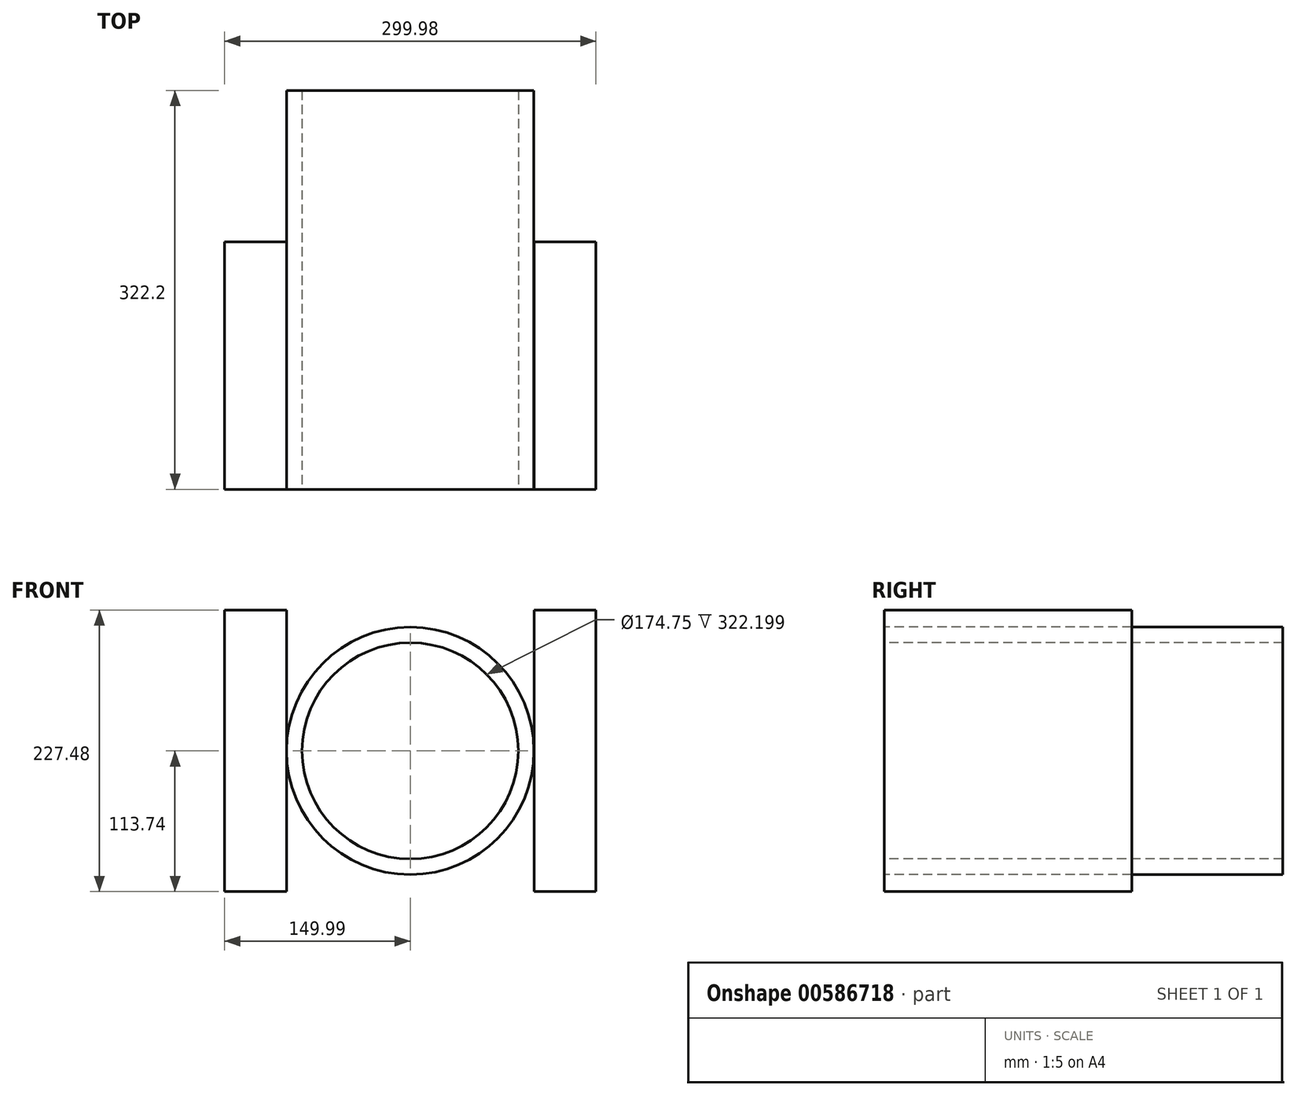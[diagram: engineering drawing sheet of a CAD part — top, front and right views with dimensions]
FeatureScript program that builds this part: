
annotation { "Feature Type Name" : "Feature", "Feature Type Description" : "" }
export const myFeature = defineFeature(function(context is Context, id is Id, definition is map)
    precondition{}
    {
        {
            var Q0;
            Q0=qCreatedBy(makeId("Front.planeOp"),FACE);
            var sketch = newSketch(context, id + "F0", { "sketchPlane" : qUnion([Q0])});
            skCircle(sketch, "E0", {"center": v(0, 0) * mm, "radius": 99.95 * mm});
            skSolve(sketch);
        }
        {
            var Q0;
            Q0=makeQuery(id+"F0.imprint","IMPRINT",FACE,{"disambiguationData":[TD([[makeQuery(id+"F0.imprint","IMPRINT",EDGE,{"derivedFrom":sQuery(id+"F0.wireOp",EDGE,"E0")}),1.0]])]});
            extrude(context, id + "F1", {"entities" : qUnion([Q0]), "oppositeDirection" : true, "depth" : 322.2 * mm, "offsetDistance" : 25.4 * mm});
        }
        {
            var Q0;
            Q0=qCreatedBy(makeId("Right.planeOp"),FACE);
            cPlane(context, id + "F2", {"entities" : qUnion([Q0]), "cplaneType" : CPlaneType.OFFSET, "offset" : 100 * mm, "width" : 152.4 * mm, "height" : 152.4 * mm});
        }
        {
            var Q0;
            Q0=qCreatedBy(id+"F2.planeOp",FACE);
            var sketch = newSketch(context, id + "F3", { "sketchPlane" : qUnion([Q0])});
            skLineSegment(sketch, "E1.bottom", {"start": v(0, 113.74) * mm, "end": v(200, 113.74) * mm});
            skLineSegment(sketch, "E1.top", {"start": v(0, -113.74) * mm, "end": v(200, -113.74) * mm});
            skLineSegment(sketch, "E1.left", {"start": v(0, 113.74) * mm, "end": v(0, -113.74) * mm});
            skLineSegment(sketch, "E1.right", {"start": v(200, 113.74) * mm, "end": v(200, -113.74) * mm});
            skSolve(sketch);
        }
        {
            var Q0;
            Q0=makeQuery(id+"F3.imprint","IMPRINT",FACE,{"disambiguationData":[TD([[makeQuery(id+"F3.imprint","IMPRINT",EDGE,{"derivedFrom":sQuery(id+"F3.wireOp",EDGE,"E1.bottom")}),-1.0]])]});
            extrude(context, id + "F4", {"entities" : qUnion([Q0]), "depth" : 50 * mm, "offsetDistance" : 25.4 * mm});
        }
        {
            var Q0;
            Q0=qCreatedBy(makeId("Right.planeOp"),FACE);
            cPlane(context, id + "F5", {"entities" : qUnion([Q0]), "cplaneType" : CPlaneType.OFFSET, "offset" : 100 * mm, "oppositeDirection" : true, "width" : 152.4 * mm, "height" : 152.4 * mm});
        }
        {
            var Q0;
            Q0=qCreatedBy(id+"F5.planeOp",FACE);
            var sketch = newSketch(context, id + "F6", { "sketchPlane" : qUnion([Q0])});
            skLineSegment(sketch, "E2.bottom", {"start": v(199.9, 113.74) * mm, "end": v(0, 113.74) * mm});
            skLineSegment(sketch, "E2.top", {"start": v(199.9, -113.59) * mm, "end": v(0, -113.59) * mm});
            skLineSegment(sketch, "E2.left", {"start": v(199.9, 113.74) * mm, "end": v(199.9, -113.59) * mm});
            skLineSegment(sketch, "E2.right", {"start": v(0, 113.74) * mm, "end": v(0, -113.59) * mm});
            skSolve(sketch);
        }
        {
            var Q0;
            Q0=makeQuery(id+"F6.imprint","IMPRINT",FACE,{"disambiguationData":[TD([[makeQuery(id+"F6.imprint","IMPRINT",EDGE,{"derivedFrom":sQuery(id+"F6.wireOp",EDGE,"E2.bottom")}),1.0]])]});
            extrude(context, id + "F7", {"entities" : qUnion([Q0]), "oppositeDirection" : true, "depth" : 50 * mm, "offsetDistance" : 25.4 * mm});
        }
        {
            var Q0;
            Q0=qCreatedBy(makeId("Front.planeOp"),FACE);
            var sketch = newSketch(context, id + "F8", { "sketchPlane" : qUnion([Q0])});
            skCircle(sketch, "E3", {"center": v(0, 0) * mm, "radius": 87.38 * mm});
            skSolve(sketch);
        }
        {
            var Q0;
            Q0 = qSketchRegion(id + "F8", true);
            extrude(context, id + "F9", {"entities" : qUnion([Q0]), "operationType" : NewBodyOperationType.REMOVE, "endBound" : BoundingType.UP_TO_NEXT, "oppositeDirection" : true, "depth" : 254 * mm, "offsetDistance" : 25.4 * mm});
        }
    });
